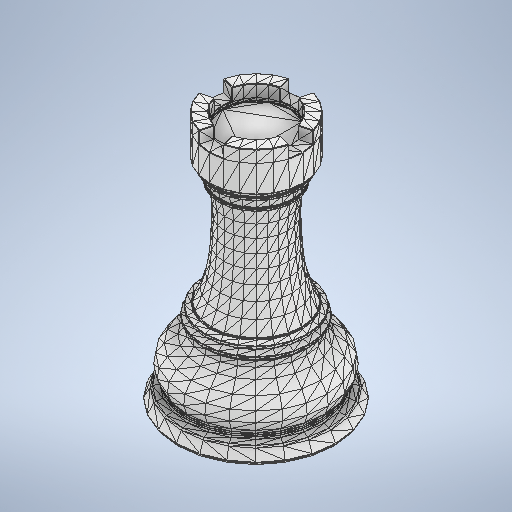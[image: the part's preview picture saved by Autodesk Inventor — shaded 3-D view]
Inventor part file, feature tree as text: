
AUTODESK INVENTOR PART (.ipt)
format: ipt  version: 2025.2 (Build 292293000, 293)  size: 5,495,296 bytes
history: native  units: mm
features: other x4, move_body x3, direct_edit x1, extrude x1, chamfer x1, sketch x1
ambient origin geometry x8: Origin, YZ Plane, XZ Plane, XY Plane, X Axis, Y Axis, Z Axis, Center Point
bodies: Body1 (feature_tree)
feature tree (11):
  other  "ChessSet v2.ipt"
  other  "Work Axis1"
  move_body  "Move Body1"
  direct_edit  "Direct Edit1"
  move_body  "Move Body2"
  extrude  "Extrusion1"  TaperAngle=90.0deg  [1 undecoded]
  chamfer  "Chamfer1"  [1 undecoded]
  other  "Solid2::ChessSet v2.ipt"
  other  "TaggingFeature1"
  sketch  "Sketch1"  dims[d0=10.0mm d1=90.0deg d2=-103.423241mm d3=0.0mm d4=-5.36425mm d5=-8.911mm d6=0.0mm d7=0.0mm d8=10.2mm d9=2.2mm d10=0.0mm d11=0.5mm d12=2.0mm d13=45.0deg]
  move_body  "Move1"
note: 2 required parameter values undecoded (feature->parameter linkage not recoverable at this tier; creation-order binding heuristic only, values carry confidence <= 0.55)
